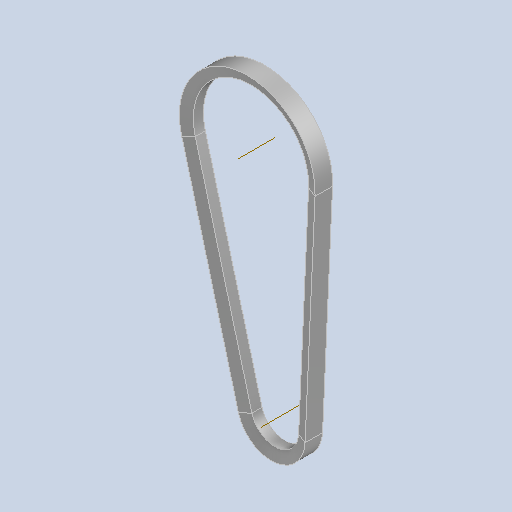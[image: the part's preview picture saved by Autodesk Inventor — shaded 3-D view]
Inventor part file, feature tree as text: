
AUTODESK INVENTOR PART (.ipt)
format: ipt  version: 2023 (Build 270158000, 158)  size: 111,104 bytes
history: native  units: mm (DEFAULTED — no unit token found)
features: other x5, sweep x1
ambient origin geometry x8: Origin, YZ Plane, XZ Plane, XY Plane, X Axis, Y Axis, Z Axis, Center Point
bodies: Solid1 (feature_tree)
feature tree (6):
  other  "Эскизная траектория"
  other  "Плоскость сечения"
  other  "РабОсь1"
  other  "РабОсь2"
  sweep  "Ремень"
  other  "Сечение"
